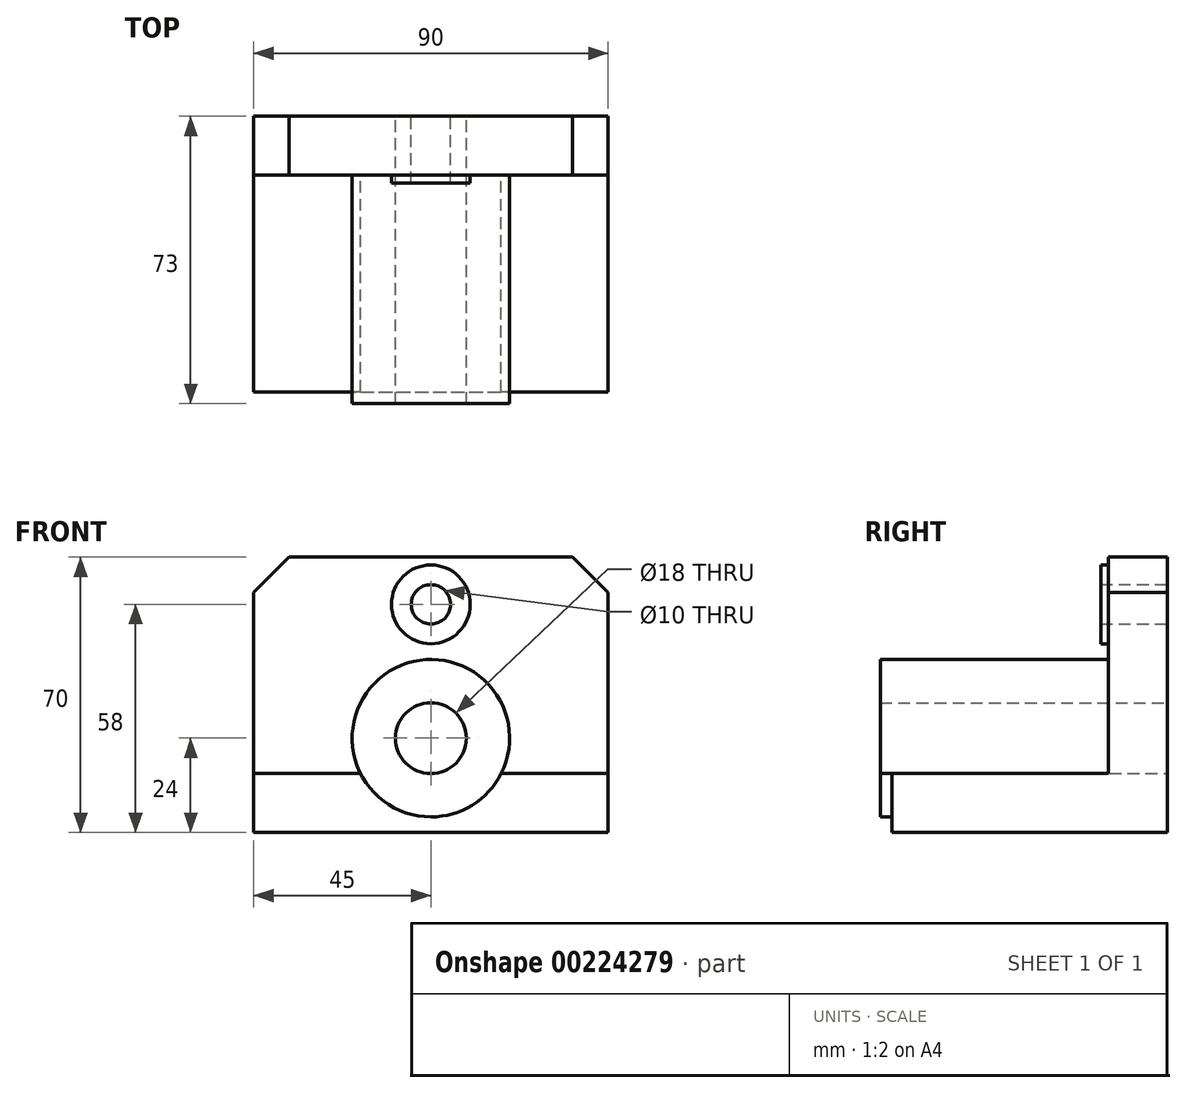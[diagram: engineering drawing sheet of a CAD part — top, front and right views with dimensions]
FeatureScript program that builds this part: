
annotation { "Feature Type Name" : "Feature", "Feature Type Description" : "" }
export const myFeature = defineFeature(function(context is Context, id is Id, definition is map)
    precondition{}
    {
        {
            var Q0;
            Q0=qCreatedBy(makeId("Front.planeOp"),FACE);
            var sketch = newSketch(context, id + "F0", { "sketchPlane" : qUnion([Q0])});
            skLineSegment(sketch, "E0", {"start": v(0, 0) * mm, "end": v(90, 0) * mm});
            skLineSegment(sketch, "E1", {"start": v(90, 0) * mm, "end": v(90, 15) * mm});
            skLineSegment(sketch, "E2", {"start": v(90, 15) * mm, "end": v(62.86, 15) * mm});
            skLineSegment(sketch, "E3", {"start": v(0, 15) * mm, "end": v(0, 0) * mm});
            skLineSegment(sketch, "E4", {"start": v(45, 70) * mm, "end": v(45, -36.01) * mm, "construction": true});
            skLineSegment(sketch, "E5", {"start": v(-8.4, 24) * mm, "end": v(112.23, 24) * mm, "construction": true});
            skCircle(sketch, "E6", {"center": v(45, 24) * mm, "radius": 20 * mm});
            skCircle(sketch, "E7", {"center": v(45, 24) * mm, "radius": 9 * mm});
            skLineSegment(sketch, "E8.trimOffspring", {"start": v(27.14, 15) * mm, "end": v(0, 15) * mm});
            skLineSegment(sketch, "E9", {"start": v(90, 15) * mm, "end": v(90, 70) * mm});
            skLineSegment(sketch, "E10", {"start": v(90, 70) * mm, "end": v(0, 70) * mm});
            skLineSegment(sketch, "E11", {"start": v(0, 70) * mm, "end": v(0, 15) * mm});
            skLineSegment(sketch, "E12", {"start": v(26.66, 58) * mm, "end": v(63.34, 58) * mm, "construction": true});
            skPoint(sketch, "E13", {"position": v(45, 58) * mm});
            skCircle(sketch, "E14", {"center": v(45, 58) * mm, "radius": 10 * mm});
            skCircle(sketch, "E15", {"center": v(45, 58) * mm, "radius": 5 * mm});
            skSolve(sketch);
        }
        {
            var Q0;
            Q0=makeQuery(id+"F0.imprint","IMPRINT",FACE,{"disambiguationData":[TD([[makeQuery(id+"F0.imprint","IMPRINT",EDGE,{"derivedFrom":sQuery(id+"F0.wireOp",EDGE,"E0")}),1.0]])]});
            extrude(context, id + "F1", {"entities" : qUnion([Q0]), "depth" : 70 * mm});
        }
        {
            var Q0;
            Q0=makeQuery(id+"F0.imprint","IMPRINT",FACE,{"disambiguationData":[TD([[makeQuery(id+"F0.imprint","IMPRINT",EDGE,{"derivedFrom":sQuery(id+"F0.wireOp",EDGE,"E7")}),-1.0]])]});
            extrude(context, id + "F2", {"entities" : qUnion([Q0]), "operationType" : NewBodyOperationType.ADD, "depth" : 73 * mm});
        }
        {
            var Q0;
            {var subQ2=sQuery(id+"F0.wireOp",EDGE,"E2");Q0=makeQuery(id+"F0.imprint","IMPRINT",FACE,{"disambiguationData":[TD([[makeQuery(id+"F0.imprint","IMPRINT",EDGE,{"derivedFrom":subQ2}),-1.0]])]});}
            extrude(context, id + "F3", {"entities" : qUnion([Q0]), "operationType" : NewBodyOperationType.ADD, "depth" : 15 * mm});
        }
        {
            var Q0;
            Q0=makeQuery(id+"F0.imprint","IMPRINT",FACE,{"disambiguationData":[TD([[makeQuery(id+"F0.imprint","IMPRINT",EDGE,{"derivedFrom":sQuery(id+"F0.wireOp",EDGE,"E14")}),1.0]])]});
            extrude(context, id + "F4", {"entities" : qUnion([Q0]), "operationType" : NewBodyOperationType.ADD, "depth" : 17 * mm});
        }
        {
            var Q0;
            Q0=makeQuery(id+"F3.opExtrude","SWEPT_EDGE",EDGE,{"disambiguationData":[OSD([sQuery(id+"F0.wireOp",EDGE,"E10"),sQuery(id+"F0.wireOp",EDGE,"E11")])]});
            var Q1;
            Q1=makeQuery(id+"F3.opExtrude","SWEPT_EDGE",EDGE,{"disambiguationData":[OSD([sQuery(id+"F0.wireOp",EDGE,"E9"),sQuery(id+"F0.wireOp",EDGE,"E10")])]});
            chamfer(context, id + "F5", {"entities" : qUnion([Q0, Q1]), "chamferType" : ChamferType.TWO_OFFSETS, "width1" : 9 * mm, "oppositeDirection" : false, "width2" : 9 * mm, "tangentPropagation" : true});
        }
    });
